# Revit family: Capsule Pool 3000-9000 приточный
name_source: partatom
category: Оборудование
units: mm (PartAtom-declared; Revit-internal decimal feet)

## family parameters
Всегда вертикально = Да
Классификация = Нет
На основе рабочей плоскости = Нет
Общий = Нет
При загрузке вырезать с полостями = Нет
Размер круглого соединителя = Использовать диаметр
Тип детали = Нормальный
Точка расчета площади = Нет

## types (7) — shared parameters
ADSK_Завод-изготовитель = ООО "Турков"
Q = 235 мм
X2 = 350 мм
В_крепежа = 10 мм
ВВ толщина = 190 мм
ВВ_от_в_кр = 78 мм
Вод подогр = Да
КА Длина = 269 мм
КА Толщина = 130 мм
КА Ширина = 160 мм
Крепеж от края = 2 мм
М2000 = Нет
М3000 = Да
Разрез от края = 310 мм
СЗ_КА = 300 мм
СЗ_фильтры = 350 мм
Толщина крышки = 50 мм
УГО_фильтр = 208 мм
вырез = 15 мм
zero-valued in all types: ADSK_Количество, ADSK_Масса

## per-type parameters (varying)
| type | A ширина | ADSK_Количество фаз | ADSK_Напряжение | ADSK_Номинальная мощность | ADSK_Расход воздуха приточный | ADSK_Свободный напор воздуха | ADSK_Ток | B высота | C глубина | X1 | ВВ высота | ВВ ширина | ВВ_выт_У | ВВ_выт_Х | ВВ_от_л_кр | ВП_модель | КА X | КА Y | СУ_У | СУ_Х |
| Capsule Pool 3000 W | 1160 мм | 1 | 220 В | 1695 Вт | 3000.0 м³/ч | 107.0 Па | 8 А | 750 мм | 450 мм | 686 мм | 600 мм | 300 мм | 300 мм | 400 мм | 221 мм | Смесительный узел 2 поворота : 3000 | 840 мм | 145 мм | 132 мм | 147 мм |
| Capsule Pool 4000 W | 1310 мм | 1 | 220 В | 1875 Вт | 4000.0 м³/ч | 273.0 Па | 9 А | 850 мм | 550 мм | 836 мм | 700 мм | 400 мм | 400 мм | 450 мм | 281 мм | Смесительный узел 2 поворота : 4000-9000 | 959 мм | 195 мм | 182 мм | 222 мм |
| Capsule Pool 5000 W | 1310 мм | 3 | 380 В | 5195 Вт | 5000.0 м³/ч | 620.0 Па | 8 А | 850 мм | 550 мм | 836 мм | 700 мм | 400 мм | 400 мм | 450 мм | 281 мм | Смесительный узел 2 поворота : 4000-9000 | 959 мм | 195 мм | 182 мм | 222 мм |
| Capsule Pool 6000 W | 1510 мм | 1 | 220 В | 3195 Вт | 6000.0 м³/ч | 132.0 Па | 15 А | 950 мм | 650 мм | 936 мм | 800 мм | 500 мм | 500 мм | 500 мм | 331 мм | Смесительный узел 2 поворота : 4000-9000 | 1059 мм | 245 мм | 232 мм | 272 мм |
| Capsule Pool 7000 W | 1510 мм | 3 | 380 В | 5650 Вт | 7000.0 м³/ч | 450.0 Па | 0 А | 950 мм | 650 мм | 936 мм | 800 мм | 500 мм | 500 мм | 500 мм | 331 мм | Смесительный узел 2 поворота : 4000-9000 | 1059 мм | 245 мм | 232 мм | 272 мм |
| Capsule Pool 8000 W | 1510 мм | 3 | 380 В | 7795 Вт | 8000.0 м³/ч | 784.0 Па | 12 А | 1050 мм | 650 мм | 1036 мм | 900 мм | 500 мм | 500 мм | 600 мм | 351 мм | Смесительный узел 2 поворота : 4000-9000 | 1159 мм | 245 мм | 232 мм | 322 мм |
| Capsule Pool 9000 W | 1510 мм | 3 | 380 В | 7894 Вт | 9000.0 м³/ч | 540.0 Па | 12 А | 1150 мм | 650 мм | 1036 мм | 1000 мм | 500 мм | 500 мм | 600 мм | 351 мм | Смесительный узел 2 поворота : 4000-9000 | 1159 мм | 245 мм | 182 мм | 322 мм |

note: column(s) folded — value = type name in every type: ADSK_Наименование

## geometry (parser evidence)
native form markers: Sweep x9
no freeform markers — native parametric forms only
